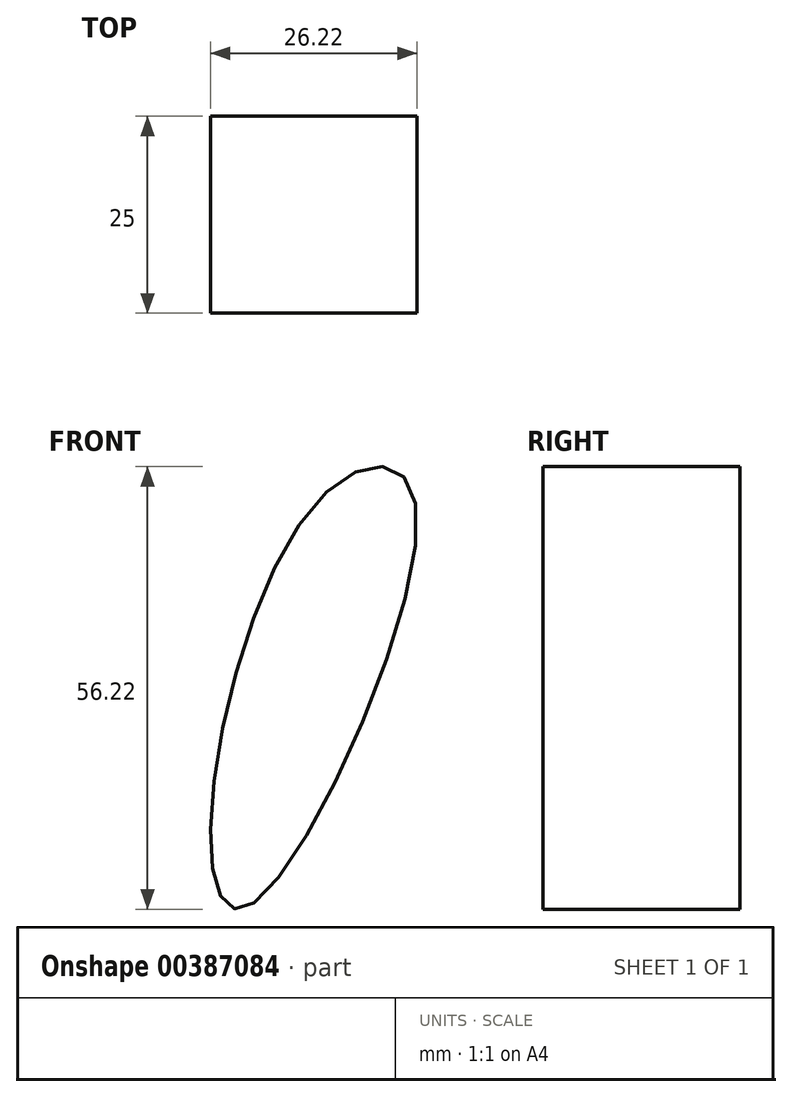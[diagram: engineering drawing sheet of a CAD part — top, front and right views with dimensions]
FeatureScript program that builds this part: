
annotation { "Feature Type Name" : "Feature", "Feature Type Description" : "" }
export const myFeature = defineFeature(function(context is Context, id is Id, definition is map)
    precondition{}
    {
        {
            var Q0;
            Q0=qCreatedBy(makeId("Front.planeOp"),FACE);
            var sketch = newSketch(context, id + "F0", { "sketchPlane" : qUnion([Q0])});
            skFitSpline(sketch, "E0", {"points": [v(-42.45, 43.73) * mm, v(-56.97, -3.59) * mm, v(-52.02, -8.71) * mm, v(-31.35, 43.39) * mm, v(-42.45, 43.73) * mm]});
            skSolve(sketch);
        }
        {
            var Q0;
            Q0=qSketchRegion(id+"F0",true);
            extrude(context, id + "F1", {"entities" : qUnion([Q0]), "depth" : 25 * mm});
        }
    });
